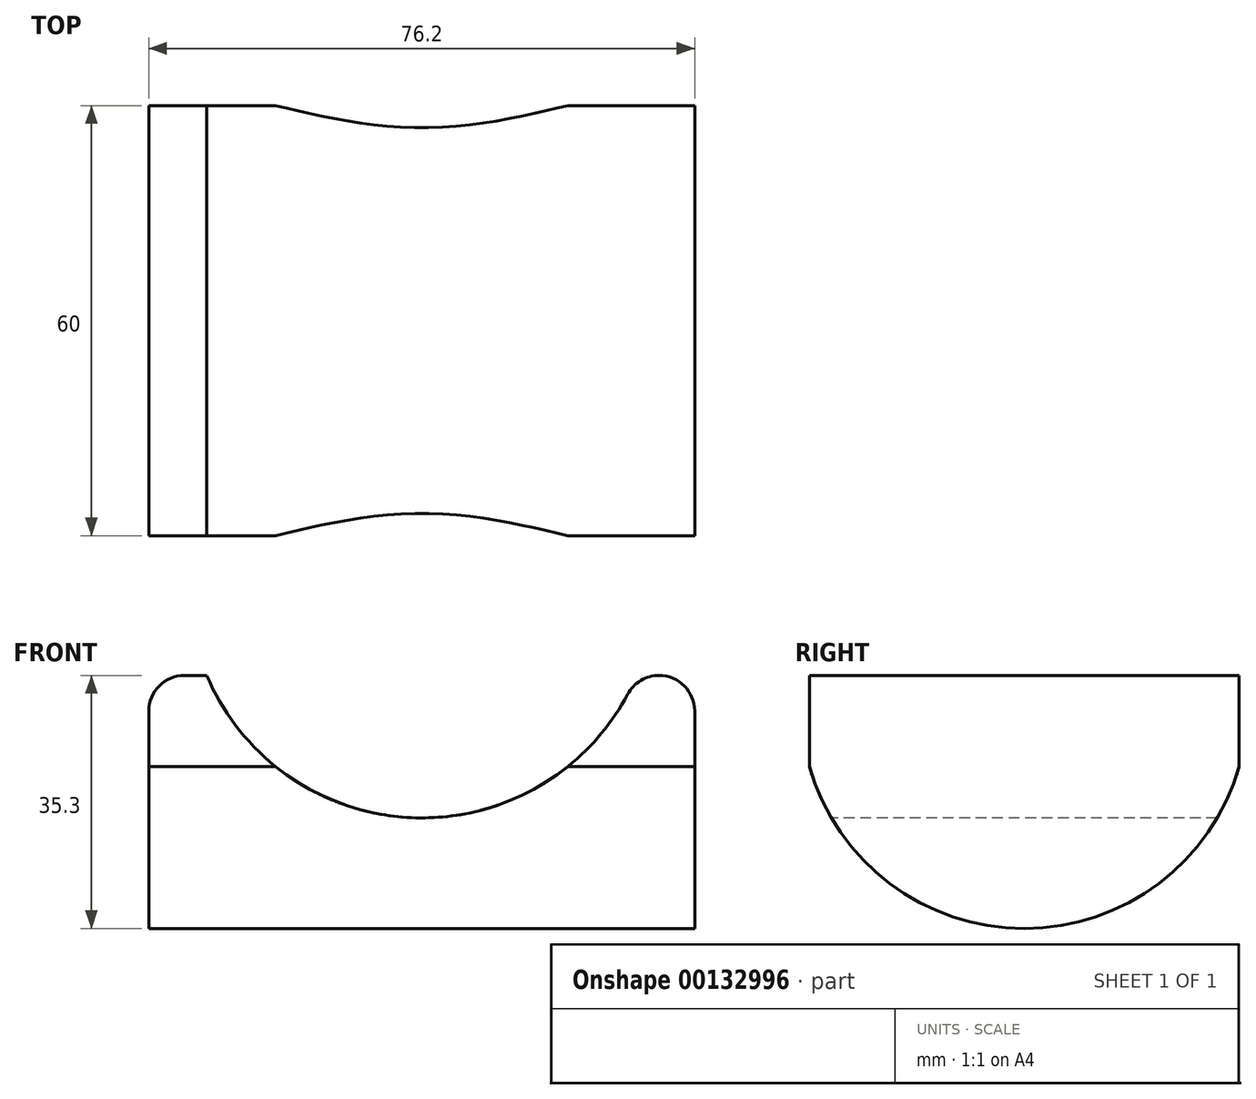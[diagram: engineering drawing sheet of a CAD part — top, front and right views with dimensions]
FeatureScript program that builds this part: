
annotation { "Feature Type Name" : "Feature", "Feature Type Description" : "" }
export const myFeature = defineFeature(function(context is Context, id is Id, definition is map)
    precondition{}
    {
        {
            var Q0;
            Q0=qCreatedBy(makeId("Right.planeOp"),FACE);
            var sketch = newSketch(context, id + "F0", { "sketchPlane" : qUnion([Q0])});
            skArc(sketch, "E0", {"start": v(-30, 0) * mm, "mid": v(0, -22.6) * mm, "end": v(30, 0) * mm});
            skLineSegment(sketch, "E1", {"start": v(-30, 0) * mm, "end": v(-30, 12.7) * mm});
            skLineSegment(sketch, "E2", {"start": v(30, 0) * mm, "end": v(30, 12.7) * mm});
            skLineSegment(sketch, "E3", {"start": v(-30, 12.7) * mm, "end": v(30, 12.7) * mm});
            skSolve(sketch);
        }
        {
            var Q0;
            Q0 = qSketchRegion(id + "F0", true);
            extrude(context, id + "F1", {"entities" : qUnion([Q0]), "depth" : 38.1 * mm, "hasSecondDirection" : true, "secondDirectionOppositeDirection" : true, "secondDirectionDepth" : 38.1 * mm});
        }
        {
            var Q0;
            Q0=qCreatedBy(makeId("Front.planeOp"),FACE);
            var sketch = newSketch(context, id + "F2", { "sketchPlane" : qUnion([Q0])});
            skArc(sketch, "E4", {"start": v(-30, 12.7) * mm, "mid": v(0, -7.18) * mm, "end": v(30, 12.7) * mm});
            skLineSegment(sketch, "E5", {"start": v(-30, 12.7) * mm, "end": v(30, 12.7) * mm});
            skSolve(sketch);
        }
        {
            var Q0;
            Q0 = qSketchRegion(id + "F2", true);
            extrude(context, id + "F3", {"entities" : qUnion([Q0]), "operationType" : NewBodyOperationType.REMOVE, "oppositeDirection" : true, "depth" : 30.48 * mm, "hasSecondDirection" : true, "secondDirectionOppositeDirection" : false, "secondDirectionDepth" : 30.48 * mm});
        }
        {
            var Q0;
            Q0=makeQuery(id+"F1.opExtrude","CAP_EDGE",EDGE,{"disambiguationData":[OSD([sQuery(id+"F0.wireOp",EDGE,"E3")])],"isStart":true});
            var Q1;
            {var subQ0=sQuery(id+"F2.wireOp",EDGE,"E5");var subQ1=sQuery(id+"F2.wireOp",EDGE,"E4");Q1=makeQuery(id+"F3.boolean.opBoolean","COPY",EDGE,{"derivedFrom":makeQuery(id+"F3.opExtrude","SWEPT_EDGE",EDGE,{"disambiguationData":[OSD([subQ1,subQ0]),TDD([makeQuery(id+"F2.imprint","INTERSECT",VERTEX,{"disambiguationData":[OD(0.0)],"derivedFrom":[subQ1,subQ0]})])]})});}
            var Q2;
            {var subQ0=sQuery(id+"F2.wireOp",EDGE,"E5");var subQ1=sQuery(id+"F2.wireOp",EDGE,"E4");Q2=makeQuery(id+"F3.boolean.opBoolean","COPY",EDGE,{"derivedFrom":makeQuery(id+"F3.opExtrude","SWEPT_EDGE",EDGE,{"disambiguationData":[OSD([subQ1,subQ0]),TDD([makeQuery(id+"F2.imprint","INTERSECT",VERTEX,{"disambiguationData":[OD(1.0)],"derivedFrom":[subQ1,subQ0]})])]})});}
            var Q3;
            Q3=makeQuery(id+"F1.opExtrude","CAP_EDGE",EDGE,{"disambiguationData":[OSD([sQuery(id+"F0.wireOp",EDGE,"E3")])],"isStart":false});
            fillet(context, id + "F4", {"entities" : qUnion([Q0, Q1, Q2, Q3]), "radius" : 5 * mm, "tangentPropagation" : true, "allowEdgeOverflow" : false});
        }
    });
